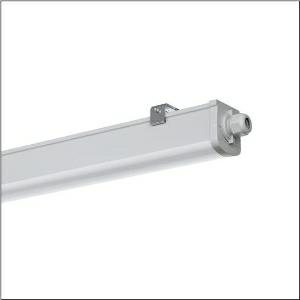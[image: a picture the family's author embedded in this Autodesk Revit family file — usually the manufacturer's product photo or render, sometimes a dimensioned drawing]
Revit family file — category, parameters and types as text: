
# Revit family: monsun_r__31_51fa20dp460b_68f5
name_source: partatom
category: Lighting Fixtures
units: mm (PartAtom-declared; Revit-internal decimal feet)

## family parameters
Cut with Voids When Loaded = No
Host = Face
Light Source = No
Part Type = Normal
Room Calculation Point = No
Round Connector Dimension = Use Diameter
Shared = No

## types (1)
- Monsun® 31 (1 x LED, 6700 lm, 50 W, 4000K)
    Apparent Load = 50 VA
    CIE Flux Codes = 42 72 91 92 100
    Color Rendering = 80
    Color Temperature = 4000K
    Default Elevation = 1800 mm
    Description = Monsun® 31, damp-proof luminaire, primary optical cover: diffuser, of PC, frosted, light emission: direct distribution, primary light characteristic: symmetric, installation type: surface-mounted, LED, rated luminous flux: 6.700lm, luminous efficacy: 134lm/W, light colour: 840, colour temperature: 4000K, control gear: ECG, with terminal, 5+1-pole, max. 2.5mm², through-wiring: 3x 2.5mm² + 3x 1.5mm², mains connection: 220..240V, AC, 50/60Hz, rated input power: 50W, housing, luminaire housing, of PC, light grey (RAL 7035), length: 1.458mm, width: 68mm, height: 76mm, protection rating (complete): IP66, insulation class (complete): insulation class II (safety insulation), certification: CE, ENEC, UKCA, protection symbol: D, impact resistance: IK08, permissible operating ambient temperature: -20..+40°C, corresponds to IFS (International Featured Standards) requirements for safety and quality in the food industry, packaging unit: 1 piece
    Height = 77 mm
    Lamp = 1 x LED
    Lamp Light Flux = 6700 lm
    Lamp Power = 50 W
    Lamp count = 1
    Length = 1518 mm
    Luminous efficacy = 134 lm/W
    Manufacturer = Siteco
    ModVariant = No
    Model = 51FA20DP460B
    Mounting Place = Ceiling
    Mounting Type = Surface mounted
    Number of Poles = 1
    OnlyDefault = Yes
    Power Factor = 1
    Product Name = Monsun® 31
    Product group = damp-proof luminaire | ceiling mounted
    ProductGroupID = 300
    Protection Class = Protection class II
    Protection Degree = IP 66
    RLX_Detail_Level = 1
    RlxData = <blob elided: 32853 chars, md5=cf8d03de>
    Socket = socket
    Standby Power = 0 W
    System Light Flux = 6700 lm
    System Power = 50 W
    Type Comments = Product without accessories
    Type Image = l_1006174.jpg
    URL = http://relux.com
    VarID = ---
    Voltage = 0 V
    Weight = 0.00 kg
    Width = 69 mm

## geometry (parser evidence)
native form markers: Blend x4, Sweep x12
no freeform markers — native parametric forms only
